FCSTD DOCUMENT  (FreeCAD 1.0R38641 +468 (Git))
Label: 1
License: All rights reserved
LicenseURL: https://en.wikipedia.org/wiki/All_rights_reserved
objects: Part::Part2DObjectPython×9, Part::Feature×1
note: 10 computed .brp shape members not serialized (recipe doc carries the construction recipe); baked Part::Feature solids carry a one-line shape summary decoded from their .brp

FEATURE [Part::Part2DObjectPython] Line  # Draft 2D object (typed FeaturePython)
  Area = 0
  ChamferSize = 0
  Closed = false
  End = (0,-10,0)
  FilletRadius = 0
  Length = 10
  MakeFace = true
  Points = (2) [(0,0,0),(0,-10,0)]
  Start = (0,0,0)
  Subdivisions = 0
FEATURE [Part::Part2DObjectPython] Line003  # Draft 2D object (typed FeaturePython)
  Area = 0
  ChamferSize = 0
  Closed = false
  End = (10,0,0)
  FilletRadius = 0
  Length = 10
  MakeFace = true
  Points = (2) [(0,0,0),(10,0,0)]
  Start = (0,0,0)
  Subdivisions = 0
FEATURE [Part::Part2DObjectPython] Line006  # Draft 2D object (typed FeaturePython)
  Area = 0
  ChamferSize = 0
  Closed = false
  End = (10,0,0)
  FilletRadius = 0
  Length = 10
  MakeFace = true
  Placement = pos=(10,-10,0) rot=(0,0,1;0rad)
  Points = (2) [(0,0,0),(0,10,0)]
  Start = (10,-10,0)
  Subdivisions = 0
FEATURE [Part::Part2DObjectPython] Line008  # Draft 2D object (typed FeaturePython)
  Area = 0
  ChamferSize = 0
  Closed = false
  End = (10,-10,0)
  FilletRadius = 0
  Length = 10
  MakeFace = true
  Placement = pos=(0,-10,0) rot=(0,0,1;0rad)
  Points = (2) [(0,0,0),(10,0,0)]
  Start = (0,-10,0)
  Subdivisions = 0
FEATURE [Part::Part2DObjectPython] Line010  # Draft 2D object (typed FeaturePython)
  Area = 0
  ChamferSize = 0
  Closed = false
  End = (10,0,0)
  FilletRadius = 0
  Length = 10
  MakeFace = true
  Placement = pos=(10,10,0) rot=(0,0,1;0rad)
  Points = (2) [(0,0,0),(0,-10,0)]
  Start = (10,10,0)
  Subdivisions = 0
FEATURE [Part::Part2DObjectPython] Line012  # Draft 2D object (typed FeaturePython)
  Area = 0
  ChamferSize = 0
  Closed = false
  End = (0,10,0)
  FilletRadius = 0
  Length = 10
  MakeFace = true
  Points = (2) [(0,0,0),(0,10,0)]
  Start = (0,0,0)
  Subdivisions = 0
FEATURE [Part::Part2DObjectPython] Line014  # Draft 2D object (typed FeaturePython)
  Area = 0
  ChamferSize = 0
  Closed = false
  End = (0,10,0)
  FilletRadius = 0
  Length = 10
  MakeFace = true
  Placement = pos=(10,10,0) rot=(0,0,1;0rad)
  Points = (2) [(0,0,0),(-10,0,0)]
  Start = (10,10,0)
  Subdivisions = 0
FEATURE [Part::Part2DObjectPython] Line016  # Draft 2D object (typed FeaturePython)
  Area = 0
  ChamferSize = 0
  Closed = false
  End = (-10,0,0)
  FilletRadius = 0
  Length = 10
  MakeFace = true
  Points = (2) [(0,0,0),(-10,0,0)]
  Start = (0,0,0)
  Subdivisions = 0
FEATURE [Part::Feature] Line017
FEATURE [Part::Part2DObjectPython] Line018  # Draft 2D object (typed FeaturePython)
  Area = 0
  ChamferSize = 0
  Closed = false
  End = (20,0,0)
  FilletRadius = 0
  Length = 10
  MakeFace = true
  Placement = pos=(10,0,0) rot=(0,0,1;0rad)
  Points = (2) [(0,0,0),(10,0,0)]
  Start = (10,0,0)
  Subdivisions = 0
